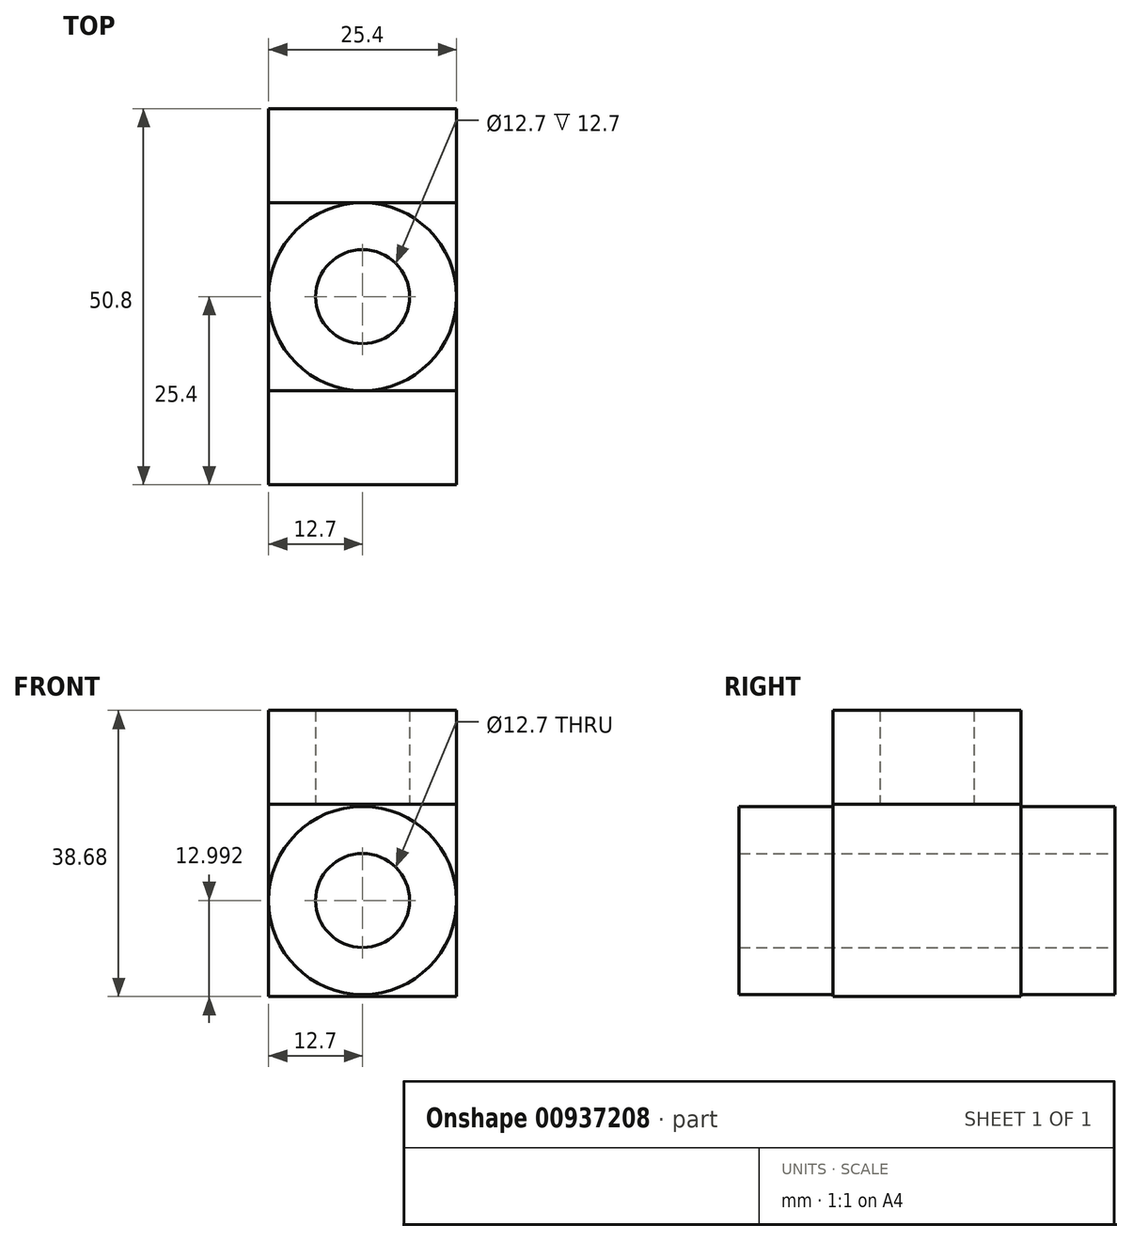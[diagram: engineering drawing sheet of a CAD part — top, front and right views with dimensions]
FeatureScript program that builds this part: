
annotation { "Feature Type Name" : "Feature", "Feature Type Description" : "" }
export const myFeature = defineFeature(function(context is Context, id is Id, definition is map)
    precondition{}
    {
        {
            var Q0;
            Q0=qCreatedBy(makeId("Top.planeOp"),FACE);
            var sketch = newSketch(context, id + "F0", { "sketchPlane" : qUnion([Q0])});
            skLineSegment(sketch, "E0.bottom", {"start": v(-12.7, 12.7) * mm, "end": v(12.7, 12.7) * mm});
            skLineSegment(sketch, "E0.top", {"start": v(-12.7, -12.7) * mm, "end": v(12.7, -12.7) * mm});
            skLineSegment(sketch, "E0.left", {"start": v(-12.7, 12.7) * mm, "end": v(-12.7, -12.7) * mm});
            skLineSegment(sketch, "E0.right", {"start": v(12.7, 12.7) * mm, "end": v(12.7, -12.7) * mm});
            skLineSegment(sketch, "E1", {"start": v(-12.7, 12.7) * mm, "end": v(12.7, -12.7) * mm, "construction": true});
            skLineSegment(sketch, "E2", {"start": v(12.7, 12.7) * mm, "end": v(-12.7, -12.7) * mm, "construction": true});
            skPoint(sketch, "E3", {"position": v(0, 0) * mm});
            skSolve(sketch);
        }
        {
            var Q0;
            Q0=makeQuery(id+"F0.imprint","IMPRINT",FACE,{"disambiguationData":[TD([[makeQuery(id+"F0.imprint","IMPRINT",EDGE,{"derivedFrom":sQuery(id+"F0.wireOp",EDGE,"E0.bottom")}),-1.0]])]});
            extrude(context, id + "F1", {"entities" : qUnion([Q0]), "depth" : 25.98 * mm, "offsetDistance" : 25.4 * mm});
        }
        {
            var Q0;
            Q0=makeQuery(id+"F1.opExtrude","CAP_FACE",FACE,{"disambiguationData":[OSD([sQuery(id+"F0.wireOp",EDGE,"E0.bottom"),sQuery(id+"F0.wireOp",EDGE,"E0.top"),sQuery(id+"F0.wireOp",EDGE,"E0.left"),sQuery(id+"F0.wireOp",EDGE,"E0.right")])],"isStart":false});
            var sketch = newSketch(context, id + "F2", { "sketchPlane" : qUnion([Q0])});
            skCircle(sketch, "E4", {"center": v(0, 0) * mm, "radius": 12.7 * mm});
            skCircle(sketch, "E5", {"center": v(0, 0) * mm, "radius": 6.35 * mm});
            skSolve(sketch);
        }
        {
            var Q0;
            Q0 = qSketchRegion(id + "F2", true);
            extrude(context, id + "F3", {"entities" : qUnion([Q0]), "operationType" : NewBodyOperationType.ADD, "depth" : 12.7 * mm, "offsetDistance" : 25.4 * mm});
        }
        {
            var Q0;
            Q0=makeQuery(id+"F1.opExtrude","SWEPT_FACE",FACE,{"disambiguationData":[OSD([sQuery(id+"F0.wireOp",EDGE,"E0.top")])]});
            var sketch = newSketch(context, id + "F4", { "sketchPlane" : qUnion([Q0])});
            skLineSegment(sketch, "E6", {"start": v(0, 0) * mm, "end": v(0, 25.98) * mm, "construction": true});
            skCircle(sketch, "E7", {"center": v(0, 13) * mm, "radius": 12.7 * mm});
            skCircle(sketch, "E8", {"center": v(0, 13) * mm, "radius": 6.35 * mm});
            skSolve(sketch);
        }
        {
            var Q0;
            Q0 = qSketchRegion(id + "F4", true);
            extrude(context, id + "F5", {"entities" : qUnion([Q0]), "operationType" : NewBodyOperationType.ADD, "depth" : 12.7 * mm, "offsetDistance" : 25.4 * mm, "hasSecondDirection" : true, "secondDirectionOppositeDirection" : true, "secondDirectionDepth" : 38.1 * mm});
        }
        {
            var Q0;
            Q0=makeQuery(id+"F5.boolean.opBoolean","SPLIT",FACE,{"disambiguationData":[TD([makeQuery(id+"F5.opExtrude","SWEPT_FACE",FACE,{"disambiguationData":[OSD([sQuery(id+"F4.wireOp",EDGE,"E8")])]})])],"derivedFrom":makeQuery(id+"F1.opExtrude","SWEPT_FACE",FACE,{"disambiguationData":[OSD([sQuery(id+"F0.wireOp",EDGE,"E0.top")])]})});
            var sketch = newSketch(context, id + "F6", { "sketchPlane" : qUnion([Q0])});
            skCircle(sketch, "E9", {"center": v(0, 13) * mm, "radius": 6.35 * mm});
            skPoint(sketch, "E9.first.point", {"position": v(-6.35, 13.1) * mm});
            skPoint(sketch, "E9.second.point", {"position": v(3.82, 7.92) * mm});
            skPoint(sketch, "E9.third.point", {"position": v(6.09, 14.8) * mm});
            skSolve(sketch);
        }
        {
            var Q0;
            Q0 = qSketchRegion(id + "F6", true);
            extrude(context, id + "F7", {"entities" : qUnion([Q0]), "operationType" : NewBodyOperationType.REMOVE, "endBound" : BoundingType.THROUGH_ALL, "oppositeDirection" : true, "depth" : 25.4 * mm, "offsetDistance" : 25.4 * mm});
        }
    });
